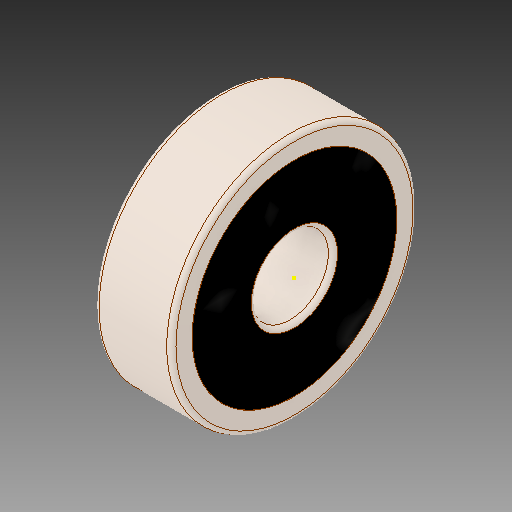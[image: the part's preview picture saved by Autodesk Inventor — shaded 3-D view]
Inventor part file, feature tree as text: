
AUTODESK INVENTOR PART (.ipt)
format: ipt  version: 2018 (Build 220112000, 112)  size: 2,076,672 bytes
history: mixed  units: mm
features: other x20, sketch x3, extrude x2, imported_body x1
ambient origin geometry x8: Origin, YZ Plane, XZ Plane, XY Plane, X Axis, Y Axis, Z Axis, Center Point
bodies: Solid1 (imported_parasolid), Solid2 (imported_parasolid), Solid3 (imported_parasolid), Solid4 (imported_parasolid), Solid5 (imported_parasolid), Solid6 (imported_parasolid), Solid7 (imported_parasolid), Solid8 (imported_parasolid), Solid9 (imported_parasolid), Solid10 (imported_parasolid), Solid11 (imported_parasolid), Solid12 (imported_parasolid), Solid13 (imported_parasolid), Solid14 (imported_parasolid), Solid15 (imported_parasolid), Solid16 (imported_parasolid), Solid17 (imported_parasolid), Solid18 (imported_parasolid), Solid19 (imported_parasolid), Solid20 (imported_parasolid)
feature tree (26):
  extrude  "Extrusion1"  Depth=0.5mm TaperAngle=0.0deg
  extrude  "Extrusion2"  [1 undecoded]
  sketch  "Sketch3"
  sketch  "Sketch1"  dims[d0=0.5mm d1=0.0mm d2=0.5mm d3=0.0mm]
  sketch  "Sketch2"
  other  "SKF 625 Inner Race^SKF 625:1"
  other  "SKF 625 Outer Race^SKF 625:1"
  other  "SKF 625 Ball^SKF 625:1"
  other  "SKF 625 Ball^SKF 625:2"
  other  "SKF 625 Ball^SKF 625:3"
  other  "SKF 625 Ball^SKF 625:4"
  other  "SKF 625 Ball^SKF 625:5"
  other  "SKF 625 Ball^SKF 625:6"
  other  "SKF 625 Ball^SKF 625:7"
  other  "SKF 625 Ball^SKF 625:8"
  other  "SKF 625 Cage^SKF 625:1"
  other  "SKF 625 Cage^SKF 625:2"
  other  "SKF 625 Cage^SKF 625:3"
  other  "SKF 625 Cage^SKF 625:4"
  other  "SKF 625 Cage^SKF 625:5"
  other  "SKF 625 Cage^SKF 625:6"
  other  "SKF 625 Cage^SKF 625:7"
  other  "SKF 625 Cage^SKF 625:8"
  other  "SKF 625 Cage^SKF 625:9"
  other  "SKF 625 Cage^SKF 625:10"
  imported_body  NMx_Import_Brep_tag  [imported B-rep: ~49 faces, bbox_mm=[0.0, 10.2, 10.2]]
note: 1 required parameter value undecoded (feature->parameter linkage not recoverable at this tier; creation-order binding heuristic only, values carry confidence <= 0.55)
